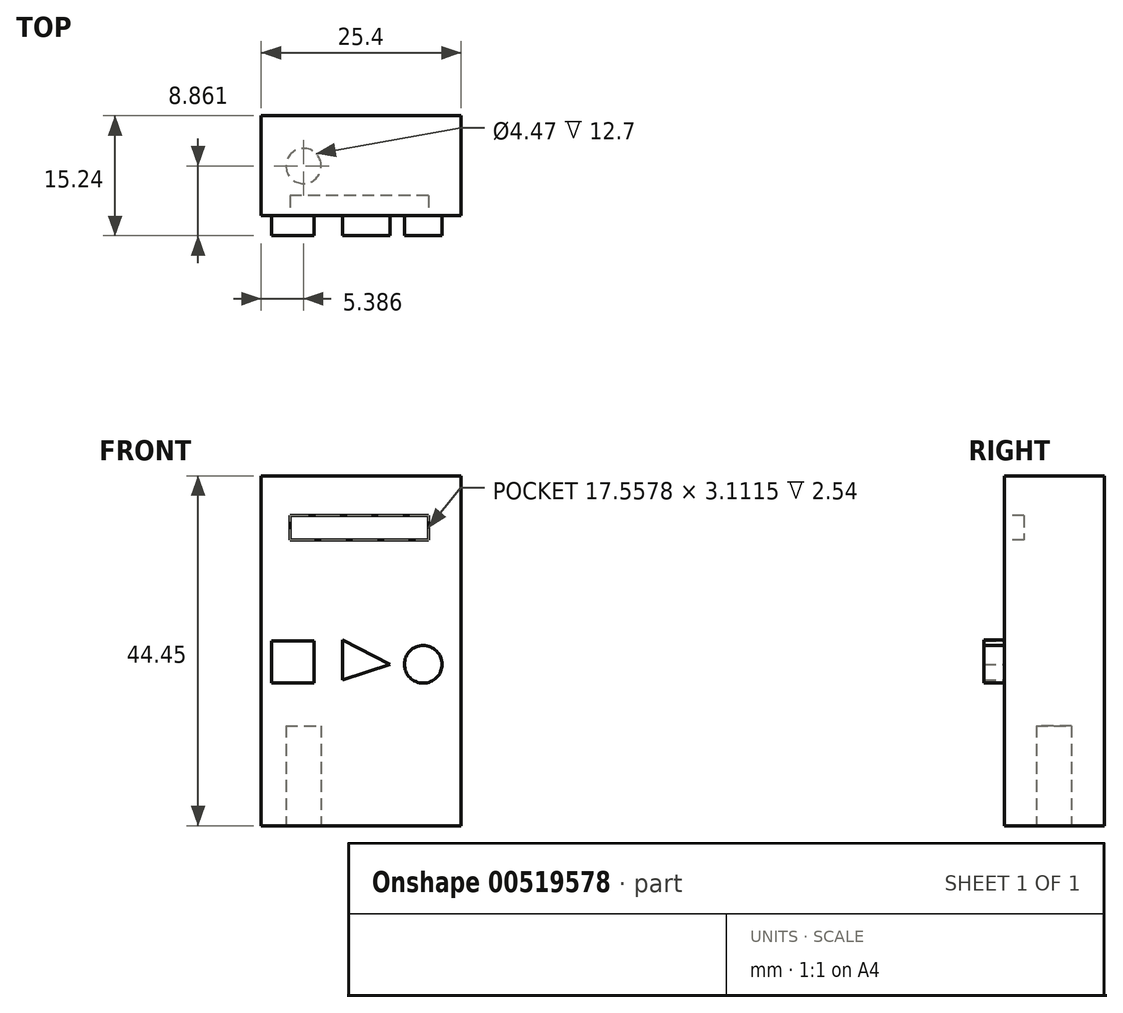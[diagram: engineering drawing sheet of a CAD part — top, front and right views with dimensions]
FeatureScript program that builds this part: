
annotation { "Feature Type Name" : "Feature", "Feature Type Description" : "" }
export const myFeature = defineFeature(function(context is Context, id is Id, definition is map)
    precondition{}
    {
        {
            var Q0;
            Q0=qCreatedBy(makeId("Front.planeOp"),FACE);
            var sketch = newSketch(context, id + "F0", { "sketchPlane" : qUnion([Q0])});
            skLineSegment(sketch, "E0", {"start": v(-14.14, 0) * mm, "end": v(-14.14, -15.4) * mm});
            skLineSegment(sketch, "E1", {"start": v(-14.14, -15.4) * mm, "end": v(11.26, -15.4) * mm});
            skLineSegment(sketch, "E2", {"start": v(11.26, -15.4) * mm, "end": v(11.26, 29.05) * mm});
            skLineSegment(sketch, "E3", {"start": v(-14.14, 0) * mm, "end": v(-14.14, 29.05) * mm});
            skLineSegment(sketch, "E4", {"start": v(-14.14, 29.05) * mm, "end": v(11.26, 29.05) * mm});
            skSolve(sketch);
        }
        {
            var Q0;
            Q0 = qSketchRegion(id + "F0", true);
            extrude(context, id + "F1", {"entities" : qUnion([Q0]), "depth" : 12.7 * mm, "offsetDistance" : 25.4 * mm});
        }
        {
            var Q0;
            Q0=makeQuery(id+"F1.opExtrude","CAP_FACE",FACE,{"disambiguationData":[OSD([sQuery(id+"F0.wireOp",EDGE,"E0"),sQuery(id+"F0.wireOp",EDGE,"E1"),sQuery(id+"F0.wireOp",EDGE,"E2"),sQuery(id+"F0.wireOp",EDGE,"E3"),sQuery(id+"F0.wireOp",EDGE,"E4")])],"isStart":false});
            var sketch = newSketch(context, id + "F2", { "sketchPlane" : qUnion([Q0])});
            skLineSegment(sketch, "E5", {"start": v(-10.45, 24) * mm, "end": v(-10.45, 20.9) * mm});
            skLineSegment(sketch, "E6", {"start": v(-10.45, 20.9) * mm, "end": v(7.11, 20.9) * mm});
            skLineSegment(sketch, "E7", {"start": v(7.11, 20.9) * mm, "end": v(7.11, 24) * mm});
            skLineSegment(sketch, "E8", {"start": v(7.11, 24) * mm, "end": v(-10.45, 24) * mm});
            skSolve(sketch);
        }
        {
            var Q0;
            Q0 = qSketchRegion(id + "F2", true);
            extrude(context, id + "F3", {"entities" : qUnion([Q0]), "operationType" : NewBodyOperationType.REMOVE, "oppositeDirection" : true, "depth" : 2.54 * mm, "offsetDistance" : 25.4 * mm});
        }
        {
            var Q0;
            Q0=makeQuery(id+"F1.opExtrude","CAP_FACE",FACE,{"disambiguationData":[OSD([sQuery(id+"F0.wireOp",EDGE,"E0"),sQuery(id+"F0.wireOp",EDGE,"E1"),sQuery(id+"F0.wireOp",EDGE,"E2"),sQuery(id+"F0.wireOp",EDGE,"E3"),sQuery(id+"F0.wireOp",EDGE,"E4")])],"isStart":false});
            var sketch = newSketch(context, id + "F4", { "sketchPlane" : qUnion([Q0])});
            skLineSegment(sketch, "E9", {"start": v(-3.78, 8.22) * mm, "end": v(-3.78, 3.11) * mm});
            skLineSegment(sketch, "E10", {"start": v(-3.78, 8.22) * mm, "end": v(2.22, 5.11) * mm});
            skLineSegment(sketch, "E11", {"start": v(-3.78, 3.11) * mm, "end": v(2.22, 5.11) * mm});
            skSolve(sketch);
        }
        {
            var Q0;
            Q0 = qSketchRegion(id + "F4", true);
            extrude(context, id + "F5", {"entities" : qUnion([Q0]), "operationType" : NewBodyOperationType.ADD, "depth" : 2.54 * mm, "offsetDistance" : 25.4 * mm});
        }
        {
            var Q0;
            Q0=makeQuery(id+"F1.opExtrude","CAP_FACE",FACE,{"disambiguationData":[OSD([sQuery(id+"F0.wireOp",EDGE,"E0"),sQuery(id+"F0.wireOp",EDGE,"E1"),sQuery(id+"F0.wireOp",EDGE,"E2"),sQuery(id+"F0.wireOp",EDGE,"E3"),sQuery(id+"F0.wireOp",EDGE,"E4")])],"isStart":false});
            var sketch = newSketch(context, id + "F6", { "sketchPlane" : qUnion([Q0])});
            skLineSegment(sketch, "E12.bottom", {"start": v(-7.45, 2.72) * mm, "end": v(-12.8, 2.72) * mm});
            skLineSegment(sketch, "E12.top", {"start": v(-7.45, 8.07) * mm, "end": v(-12.8, 8.07) * mm});
            skLineSegment(sketch, "E12.left", {"start": v(-7.45, 2.72) * mm, "end": v(-7.45, 8.07) * mm});
            skLineSegment(sketch, "E12.right", {"start": v(-12.8, 2.72) * mm, "end": v(-12.8, 8.07) * mm});
            skPoint(sketch, "E12.middle", {"position": v(-10.13, 5.4) * mm});
            skSolve(sketch);
        }
        {
            var Q0;
            Q0 = qSketchRegion(id + "F6", true);
            extrude(context, id + "F7", {"entities" : qUnion([Q0]), "operationType" : NewBodyOperationType.ADD, "depth" : 2.54 * mm, "offsetDistance" : 25.4 * mm});
        }
        {
            var Q0;
            Q0=makeQuery(id+"F1.opExtrude","CAP_FACE",FACE,{"disambiguationData":[OSD([sQuery(id+"F0.wireOp",EDGE,"E0"),sQuery(id+"F0.wireOp",EDGE,"E1"),sQuery(id+"F0.wireOp",EDGE,"E2"),sQuery(id+"F0.wireOp",EDGE,"E3"),sQuery(id+"F0.wireOp",EDGE,"E4")])],"isStart":false});
            var sketch = newSketch(context, id + "F8", { "sketchPlane" : qUnion([Q0])});
            skCircle(sketch, "E13", {"center": v(6.45, 5.11) * mm, "radius": 2.39 * mm});
            skSolve(sketch);
        }
        {
            var Q0;
            Q0 = qSketchRegion(id + "F8", true);
            extrude(context, id + "F9", {"entities" : qUnion([Q0]), "operationType" : NewBodyOperationType.ADD, "depth" : 2.54 * mm, "offsetDistance" : 25.4 * mm});
        }
        {
            var Q0;
            Q0=makeQuery(id+"F1.opExtrude","SWEPT_FACE",FACE,{"disambiguationData":[OSD([sQuery(id+"F0.wireOp",EDGE,"E1")])]});
            var sketch = newSketch(context, id + "F10", { "sketchPlane" : qUnion([Q0])});
            skCircle(sketch, "E14", {"center": v(-8.75, 6.38) * mm, "radius": 2.24 * mm});
            skSolve(sketch);
        }
        {
            var Q0;
            Q0 = qSketchRegion(id + "F10", true);
            extrude(context, id + "F11", {"entities" : qUnion([Q0]), "operationType" : NewBodyOperationType.REMOVE, "oppositeDirection" : true, "depth" : 12.7 * mm, "offsetDistance" : 25.4 * mm});
        }
    });
